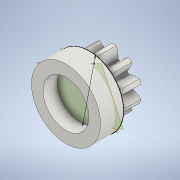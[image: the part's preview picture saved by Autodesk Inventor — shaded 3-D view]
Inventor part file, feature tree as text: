
AUTODESK INVENTOR PART (.ipt)
format: ipt  version: 2022 (Build 260153070, 153G)  size: 355,328 bytes
history: native  units: mm (DEFAULTED — no unit token found)
features: sketch x7, other x6, extrude x5, plane x5
ambient origin geometry x8: Origin, YZ Plane, XZ Plane, XY Plane, X Axis, Y Axis, Z Axis, Center Point
bodies: Solid1 (feature_tree)
feature tree (23):
  extrude  "Extrusion1"  Depth=3.0mm TaperAngle=0.0deg
  plane  "Work Plane2"
  plane  "Work Plane8"
  plane  "Work Plane9"
  other  "Spur Gear"
  plane  "Work Plane12"
  plane  "Work Plane14"
  extrude  "Extrusion4"  Depth=10.0mm TaperAngle=0.0deg
  extrude  "Extrusion3"  Depth=3.141593mm TaperAngle=0.0deg
  extrude  "Extrusion5"  TaperAngle=0.0deg  [1 undecoded]
  extrude  "Extrusion6"  Depth=21.0mm
  sketch  "Sketch9"  dims[d53=6.0mm d54=20.0mm d55=0.0mm d60=9.0mm d61=3.0mm d62=0.0mm d63=3.0mm d64=0.0mm d65=2.2mm d66=3.0mm d67=0.0mm]
  sketch  "Sketch1"  dims[d0=7.2mm d1=3.0mm d2=0.0mm]
  sketch  "Sketch2"  dims[d3=6.0mm d4=10.0mm d5=0.0mm]
  other  "Srf1"
  sketch  "Sketch5"  dims[d16=21.0mm d17=0.0mm d34=3.141593mm]
  sketch  "Sketch6"  dims[d39=0.0mm d41=0.0mm]
  sketch  "Sketch7"  dims[d43=21.0mm d46=21.0mm]
  sketch  "Sketch8"  dims[d47=0.0mm d48=0.0mm]
  other  "Pitch Diameter"
  other  "<userpath> laptop\Desktop\SumoBot\sumobotLIDAR\sumobotLIDAR.iam"
  other  "sumobotLIDAR.iam"
  other  "Magnet:1"
note: 1 required parameter value undecoded (feature->parameter linkage not recoverable at this tier; creation-order binding heuristic only, values carry confidence <= 0.55)
